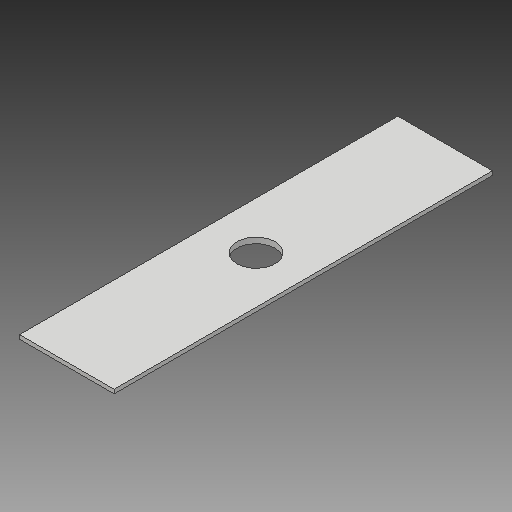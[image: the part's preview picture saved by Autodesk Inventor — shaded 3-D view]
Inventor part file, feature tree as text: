
AUTODESK INVENTOR PART (.ipt)
format: ipt  version: 2017 (Build 210142000, 142)  size: 102,400 bytes
history: native  units: mm
features: sketch x3, extrude x2, hole x1, projected_geometry x1
ambient origin geometry x8: Origin, YZ Plane, XZ Plane, XY Plane, X Axis, Y Axis, Z Axis, Center Point
bodies: Solid1 (feature_tree)
feature tree (7):
  extrude  "Cuerpo"  Depth=50.0mm
  extrude  "Ranura"  Depth=3.2mm
  hole  "Rueda Externa"  [1 undecoded]
  sketch  "Sketch1"  dims[d0=200.0mm d1=50.0mm]
  sketch  "Sketch2"  dims[d2=2.1mm d3=0.0mm d4=3.2mm]
  projected_geometry  "Projected Loop1"
  sketch  "Sketch4"  dims[d5=0.9mm d6=0.0mm d8=20.2mm d9=6.0mm d10=4.0mm d11=2.0mm d12=90.0deg d13=8.0mm d14=20.594885mm]
note: 1 required parameter value undecoded (feature->parameter linkage not recoverable at this tier; creation-order binding heuristic only, values carry confidence <= 0.55)
